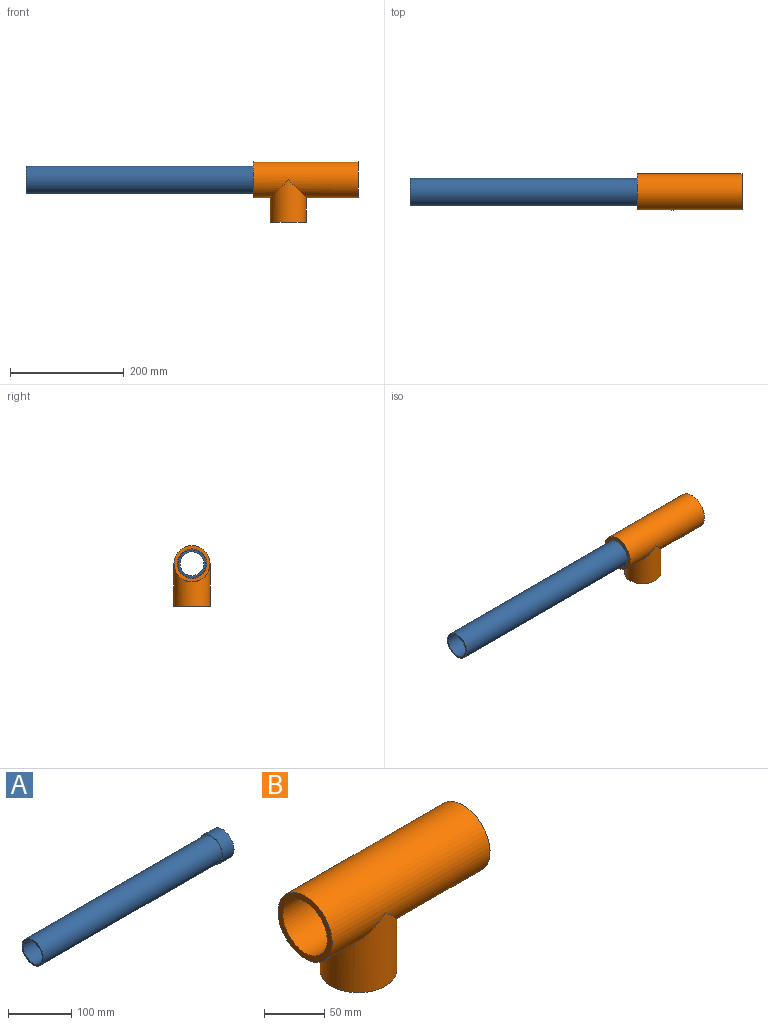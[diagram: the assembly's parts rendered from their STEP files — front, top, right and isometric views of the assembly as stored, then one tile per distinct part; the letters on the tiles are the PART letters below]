
ASSEMBLY  parts=2 mates=1
PART A: 6 faces, bbox 425x52x52 mm
  f0: cylinder r=21mm len=425mm, axis (-1,0,0), area 56077.4mm2, adj f2,f5
  f1: cylinder r=26mm len=52mm, axis (-1,0,0), area 4084.1mm2, adj f2,f3
  f2: plane 52x52mm, normal (1,0,0), area 738.3mm2, adj f0,f1
  f3: plane 52x52mm, normal (-1,0,0), area 294.5mm2, adj f1,f4
  f4: cylinder r=24.13mm len=400mm, axis (1,0,0), area 60645.3mm2, adj f3,f5
  f5: plane 48.26x48.26mm, normal (-1,0,0), area 443.8mm2, adj f0,f4
PART B: 7 faces, bbox 185x63.5x106.8 mm
  f0: cylinder r=26mm len=185mm, axis (1,0,0), area 27518.1mm2, adj f2,f3,f6
  f1: cylinder r=31.75mm len=185mm, axis (1,0,0), area 32873.6mm2, adj f3,f5,f6
  f2: cylinder r=26mm len=75mm, axis (0,0,-1), area 9548.2mm2, adj f0,f4
  f3: plane 63.5x63.5mm, normal (-1,0,0), area 1043.2mm2, adj f0,f1
  f4: plane 63.5x63.5mm, normal (0,0,-1), area 1043.2mm2, adj f2,f5
  f5: cylinder r=31.75mm len=75mm, axis (0,0,1), area 10929.6mm2, adj f1,f4
  f6: plane 63.5x63.5mm, normal (1,0,0), area 1043.2mm2, adj f0,f1
PLACE A t=(137.44,-13.81,76.73)mm
PLACE B t=(137.44,-13.81,76.73)mm
MATE fastened B.f0 <-> A.f1  axis (1,0,0) through (12.44,-13.81,76.73)mm
